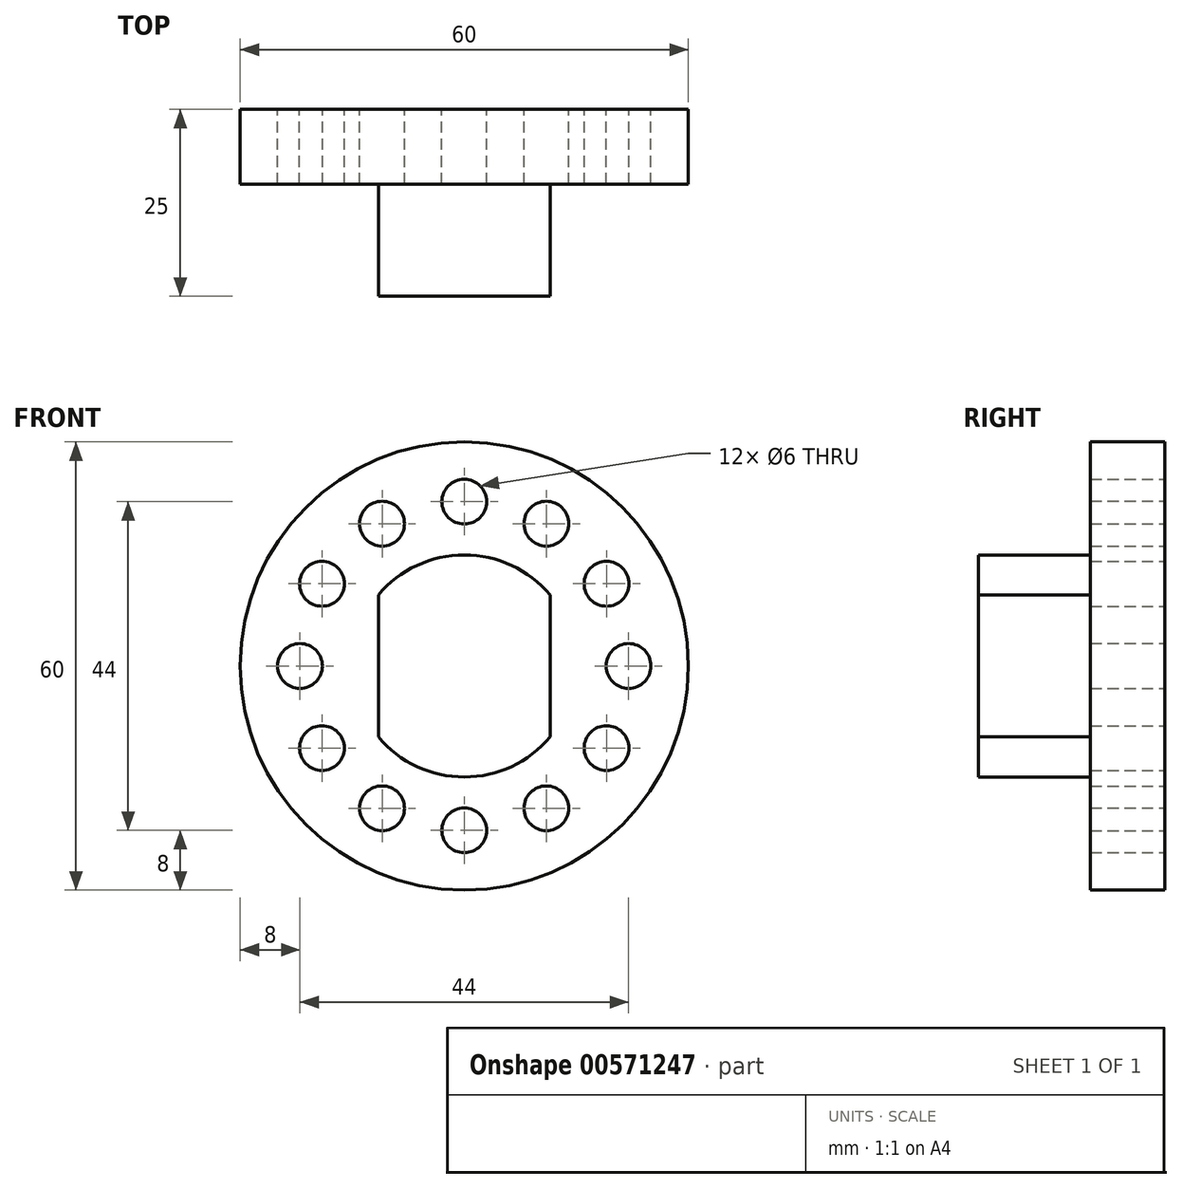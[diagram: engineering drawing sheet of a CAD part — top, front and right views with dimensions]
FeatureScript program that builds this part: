
annotation { "Feature Type Name" : "Feature", "Feature Type Description" : "" }
export const myFeature = defineFeature(function(context is Context, id is Id, definition is map)
    precondition{}
    {
        {
            var Q0;
            Q0=qCreatedBy(makeId("Front.planeOp"),FACE);
            var sketch = newSketch(context, id + "F0", { "sketchPlane" : qUnion([Q0])});
            skCircle(sketch, "E0", {"center": v(0, 0) * mm, "radius": 30 * mm});
            skCircle(sketch, "E1", {"center": v(0, 0) * mm, "radius": 22 * mm});
            skCircle(sketch, "E2", {"center": v(0, 22) * mm, "radius": 3 * mm});
            skCircle(sketch, "E3.1.1", {"center": v(-11, 19.05) * mm, "radius": 3 * mm});
            skCircle(sketch, "E3.2.1", {"center": v(-19.05, 11) * mm, "radius": 3 * mm});
            skCircle(sketch, "E3.3.1", {"center": v(-22, 0) * mm, "radius": 3 * mm});
            skCircle(sketch, "E3.4.1", {"center": v(-19.05, -11) * mm, "radius": 3 * mm});
            skCircle(sketch, "E3.5.1", {"center": v(-11, -19.05) * mm, "radius": 3 * mm});
            skCircle(sketch, "E3.6.1", {"center": v(0, -22) * mm, "radius": 3 * mm});
            skCircle(sketch, "E3.7.1", {"center": v(11, -19.05) * mm, "radius": 3 * mm});
            skCircle(sketch, "E3.8.1", {"center": v(19.05, -11) * mm, "radius": 3 * mm});
            skCircle(sketch, "E3.9.1", {"center": v(22, 0) * mm, "radius": 3 * mm});
            skCircle(sketch, "E3.10.1", {"center": v(19.05, 11) * mm, "radius": 3 * mm});
            skCircle(sketch, "E3.11.1", {"center": v(11, 19.05) * mm, "radius": 3 * mm});
            skLineSegment(sketch, "E3.anchor1", {"start": v(0, 0) * mm, "end": v(0, 22) * mm, "construction": true});
            skLineSegment(sketch, "E3.anchor2", {"start": v(0, 0) * mm, "end": v(11, 19.05) * mm, "construction": true});
            skLineSegment(sketch, "E4.left", {"start": v(-11.5, 9.5) * mm, "end": v(-11.5, -9.5) * mm});
            skLineSegment(sketch, "E4.right", {"start": v(11.5, 9.5) * mm, "end": v(11.5, -9.5) * mm});
            skArc(sketch, "E5", {"start": v(11.5, 9.5) * mm, "mid": v(0, 14.87) * mm, "end": v(-11.5, 9.5) * mm});
            skArc(sketch, "E6", {"start": v(-11.5, -9.5) * mm, "mid": v(0, -14.87) * mm, "end": v(11.5, -9.5) * mm});
            skSolve(sketch);
        }
        {
            var Q0;
            Q0=makeQuery(id+"F0.imprint","IMPRINT",FACE,{"disambiguationData":[TD([[makeQuery(id+"F0.imprint","IMPRINT",EDGE,{"derivedFrom":sQuery(id+"F0.wireOp",EDGE,"E0")}),1.0]])]});
            var Q1;
            Q1=makeQuery(id+"F0.imprint","IMPRINT",FACE,{"disambiguationData":[TD([[makeQuery(id+"F0.imprint","IMPRINT",EDGE,{"derivedFrom":sQuery(id+"F0.wireOp",EDGE,"E4.left")}),-1.0]])]});
            extrude(context, id + "F1", {"entities" : qUnion([Q0, Q1]), "depth" : 10 * mm, "offsetDistance" : 25 * mm});
        }
        {
            var Q0;
            Q0=makeQuery(id+"F0.imprint","IMPRINT",FACE,{"disambiguationData":[TD([[makeQuery(id+"F0.imprint","IMPRINT",EDGE,{"derivedFrom":sQuery(id+"F0.wireOp",EDGE,"E4.left")}),1.0]])]});
            extrude(context, id + "F2", {"entities" : qUnion([Q0]), "operationType" : NewBodyOperationType.ADD, "depth" : 25 * mm, "offsetDistance" : 25 * mm});
        }
    });
